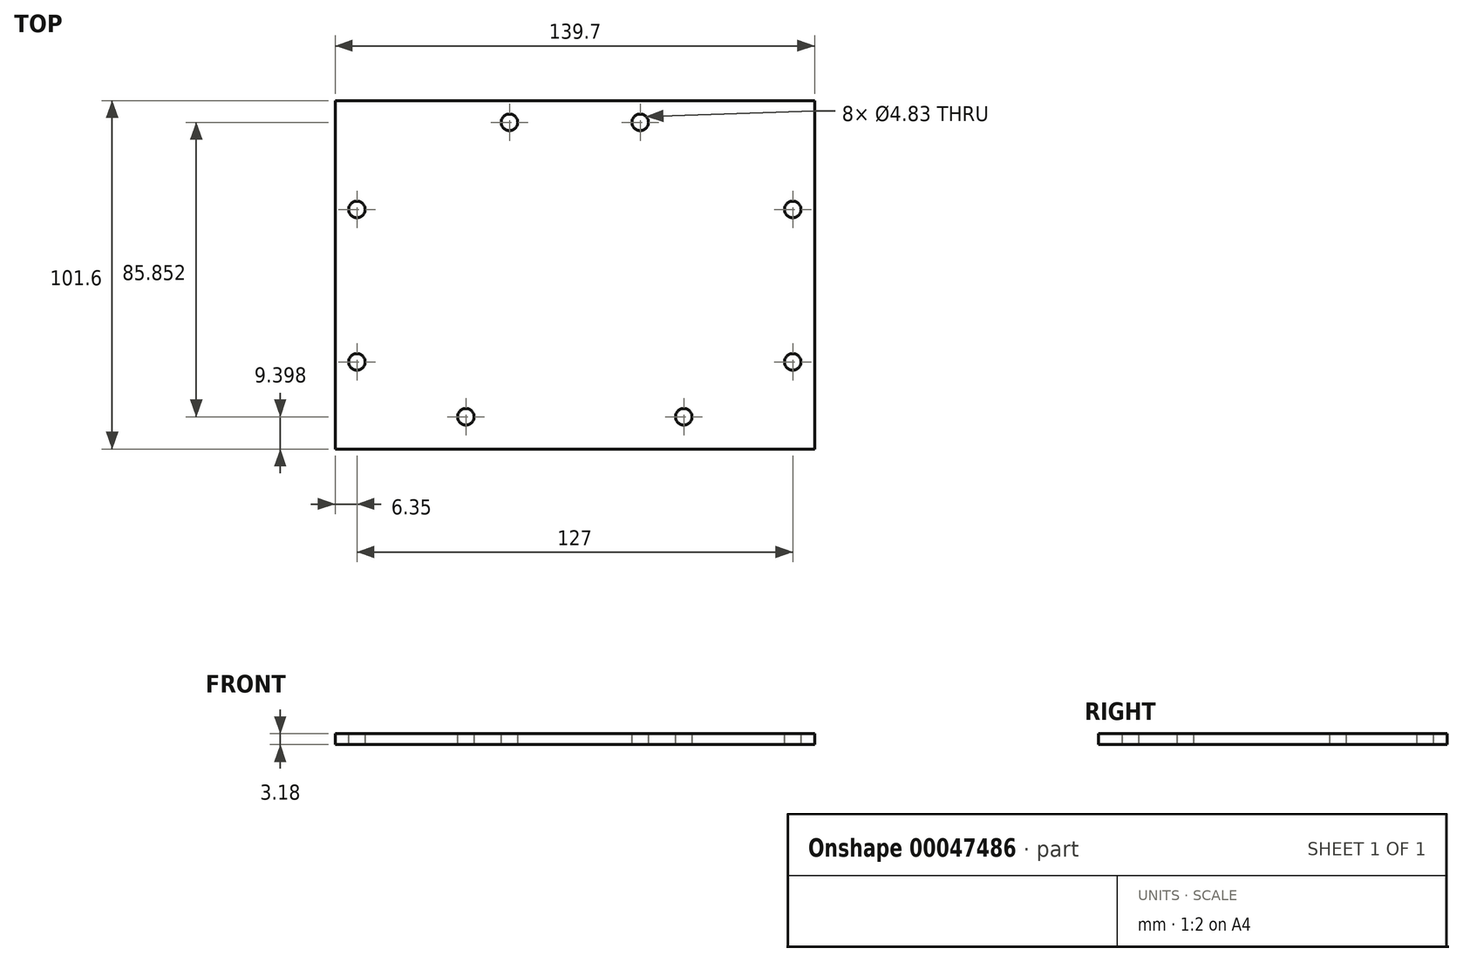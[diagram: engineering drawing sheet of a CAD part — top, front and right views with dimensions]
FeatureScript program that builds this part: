
annotation { "Feature Type Name" : "Feature", "Feature Type Description" : "" }
export const myFeature = defineFeature(function(context is Context, id is Id, definition is map)
    precondition{}
    {
        {
            var Q0;
            Q0=qCreatedBy(makeId("Top.planeOp"),FACE);
            var sketch = newSketch(context, id + "F0", { "sketchPlane" : qUnion([Q0])});
            skLineSegment(sketch, "E0.rect.bottom", {"start": v(-69.85, 50.8) * mm, "end": v(69.85, 50.8) * mm});
            skLineSegment(sketch, "E0.rect.top", {"start": v(-69.85, -50.8) * mm, "end": v(69.85, -50.8) * mm});
            skLineSegment(sketch, "E0.rect.left", {"start": v(-69.85, 50.8) * mm, "end": v(-69.85, -50.8) * mm});
            skLineSegment(sketch, "E0.rect.right", {"start": v(69.85, 50.8) * mm, "end": v(69.85, -50.8) * mm});
            skPoint(sketch, "E0.rect.middle", {"position": v(0, 0) * mm});
            skSolve(sketch);
        }
        {
            var Q0;
            Q0 = qSketchRegion(id + "F0", true);
            extrude(context, id + "F1", {"entities" : qUnion([Q0]), "depth" : 3.17 * mm, "symmetric" : true});
        }
        {
            var Q0;
            Q0=makeQuery(id+"F1.opExtrude","CAP_FACE",FACE,{"disambiguationData":[OSD([sQuery(id+"F0.wireOp",EDGE,"E0.rect.bottom"),sQuery(id+"F0.wireOp",EDGE,"E0.rect.top"),sQuery(id+"F0.wireOp",EDGE,"E0.rect.left"),sQuery(id+"F0.wireOp",EDGE,"E0.rect.right")])],"isStart":false});
            var sketch = newSketch(context, id + "F2", { "sketchPlane" : qUnion([Q0])});
            skCircle(sketch, "E1", {"center": v(-19.05, 44.45) * mm, "radius": 2.41 * mm});
            skCircle(sketch, "E2", {"center": v(19.05, 44.45) * mm, "radius": 2.41 * mm});
            skCircle(sketch, "E3", {"center": v(-63.5, 19.05) * mm, "radius": 2.41 * mm});
            skCircle(sketch, "E4", {"center": v(-63.5, -25.4) * mm, "radius": 2.41 * mm});
            skCircle(sketch, "E5.MirrorC", {"center": v(63.5, 19.05) * mm, "radius": 2.41 * mm});
            skCircle(sketch, "E6.MirrorC", {"center": v(63.5, -25.4) * mm, "radius": 2.41 * mm});
            skCircle(sketch, "E7", {"center": v(-31.75, -41.4) * mm, "radius": 2.41 * mm});
            skCircle(sketch, "E8", {"center": v(31.75, -41.4) * mm, "radius": 2.41 * mm});
            skSolve(sketch);
        }
        {
            var Q0;
            Q0 = qSketchRegion(id + "F2", true);
            extrude(context, id + "F3", {"entities" : qUnion([Q0]), "operationType" : NewBodyOperationType.REMOVE, "oppositeDirection" : true, "depth" : 3.17 * mm});
        }
    });
